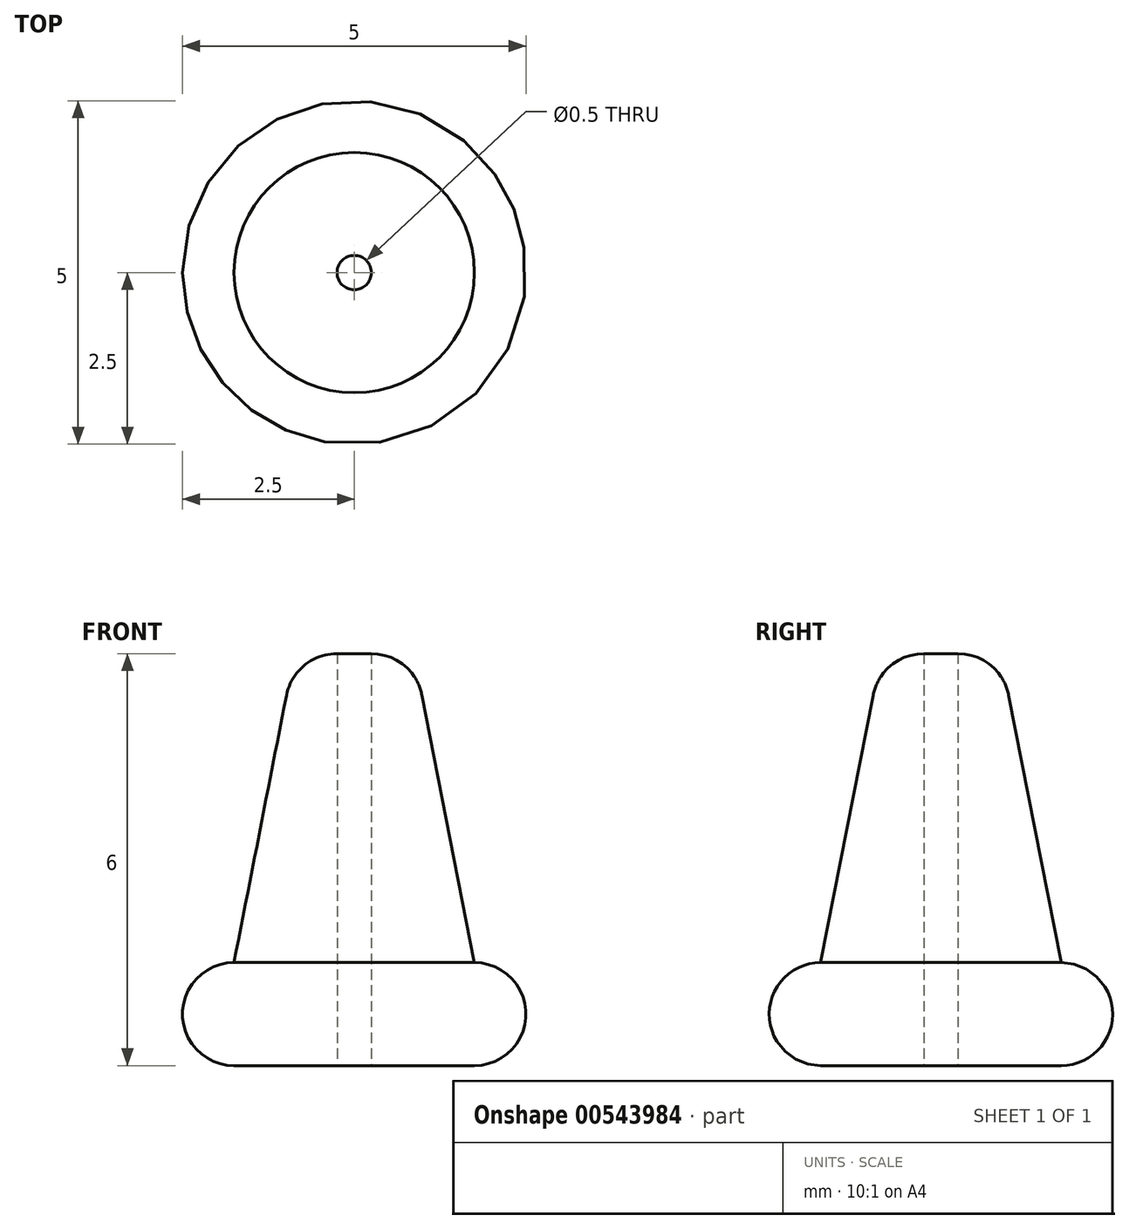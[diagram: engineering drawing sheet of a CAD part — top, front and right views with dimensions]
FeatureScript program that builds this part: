
annotation { "Feature Type Name" : "Feature", "Feature Type Description" : "" }
export const myFeature = defineFeature(function(context is Context, id is Id, definition is map)
    precondition{}
    {
        {
            var Q0;
            Q0=qCreatedBy(makeId("Front.planeOp"),FACE);
            var sketch = newSketch(context, id + "F0", { "sketchPlane" : qUnion([Q0])});
            skLineSegment(sketch, "E0", {"start": v(0.25, 0) * mm, "end": v(0.25, 6) * mm});
            skLineSegment(sketch, "E1", {"start": v(0.25, 0) * mm, "end": v(1.75, 0) * mm});
            skArc(sketch, "E2", {"start": v(1.75, 0) * mm, "mid": v(2.5, 0.75) * mm, "end": v(1.75, 1.5) * mm});
            skLineSegment(sketch, "E3", {"start": v(1.75, 0) * mm, "end": v(1.75, 1.5) * mm, "construction": true});
            skLineSegment(sketch, "E4", {"start": v(1.75, 1.5) * mm, "end": v(0.99, 5.4) * mm});
            skArc(sketch, "E5", {"start": v(0.99, 5.4) * mm, "mid": v(0.73, 5.83) * mm, "end": v(0.25, 6) * mm});
            skLineSegment(sketch, "E6", {"start": v(0, 0) * mm, "end": v(0, 8.8) * mm});
            skSolve(sketch);
        }
        {
            var Q0;
            Q0=makeQuery(id+"F0.imprint","IMPRINT",FACE,{"disambiguationData":[TD([[makeQuery(id+"F0.imprint","IMPRINT",EDGE,{"derivedFrom":sQuery(id+"F0.wireOp",EDGE,"E0")}),-1.0]])]});
            var Q1;
            Q1=sQuery(id+"F0.wireOp",EDGE,"E6");
            revolve(context, id + "F1", {"entities" : qUnion([Q0]), "axis" : qUnion([Q1]), "revolveType" : RevolveType.FULL});
        }
    });
